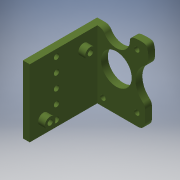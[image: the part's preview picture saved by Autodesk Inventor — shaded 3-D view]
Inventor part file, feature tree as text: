
AUTODESK INVENTOR PART (.ipt)
format: ipt  version: 2018 (Build 220112000, 112)  size: 273,408 bytes
history: native  units: in
note: dims shown in document units (in); Inventor stores cm internally (conversion verified against a paired STEP export)
features: extrude x11, sketch x9, other x3, fillet x1, projected_geometry x1, reference x1
ambient origin geometry x8: Origin, YZ Plane, XZ Plane, XY Plane, X Axis, Y Axis, Z Axis, Center Point
bodies: Solid1 (feature_tree)
feature tree (26):
  sketch  "Sketch1"  dims[d0=0.385in d1=0.385in]
  extrude  "Extrusion1"  Depth=0.385in
  extrude  "Extrusion2"  Depth=0.5in
  extrude  "Extrusion3"  Depth=0.5in
  extrude  "Extrusion4"  Depth=0.25in TaperAngle=0.0deg
  sketch  "Sketch4"  dims[d8=0.5in d9=0.25in d10=0.0in]
  extrude  "Extrusion5"  Depth=0.5in
  extrude  "Extrusion7"  Depth=2.0in
  extrude  "Extrusion8"  Depth=0.25in
  extrude  "Extrusion9"  Depth=1.036in
  fillet  "Fillet2"  Radius=1.122in
  extrude  "Extrusion10"  Depth=0.25in
  extrude  "Extrusion11"  Depth=2.0in
  extrude  "Extrusion12"  Depth=0.25in
  sketch  "Sketch2"  dims[d4=2.08in d5=0.5in]
  sketch  "Sketch3"  dims[d6=0.5in d7=0.5in]
  projected_geometry  "Projected Loop1"
  sketch  "Sketch5"  dims[d11=0.5in d12=0.0in d13=0.1935in]
  sketch  "Sketch6"  dims[d14=0.5in d15=0.0in d16=2.0in]
  sketch  "Sketch8"  dims[d17=0.25in d18=0.0in d19=0.768in]
  sketch  "Sketch9"  dims[d20=0.699in d21=1.036in d22=1.122in]
  sketch  "Sketch10"  dims[d23=2.5in d24=0.0in d25=0.25in d26=2.0in d27=0.25in d30=0.5in d31=0.95in d32=0.125in d33=0.1935in d38=1.0in d39=0.0in d40=0.75in d42=0.4in d43=1.0in d44=0.0in d46=1.25in d47=1.25in d48=1.25in d49=1.25in d50=2.0in d51=1.0in d54=1.0in d55=0.0in d56=0.25in d57=1.0in d58=1.25in d59=0.75in d60=0.25in d61=0.125in d62=0.5in d63=1.0in d64=0.0in d65=0.25in d66=0.25in d67=0.2in d68=1.9685in d70=0.5in d71=0.3937in d73=1.0in d75=1.0in d76=0.0in d77=0.1935in d78=0.25in d79=0.25in d80=1.9685in d82=0.5in d83=0.3937in d85=1.0in d87=1.0in d88=0.0in]
  reference  "Reference1"
  parser-record x1  (decoder bookkeeping rows leaked as tree rows — omitted from the tree; the rows remain in map.json)
  other  "Wheel Assembly Right.iam"
  other  "mounting plate:1"
note: 1 file-system path scrubbed to <path> (originals preserved in map.json)
